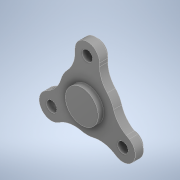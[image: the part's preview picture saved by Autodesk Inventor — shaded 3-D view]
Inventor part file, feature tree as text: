
AUTODESK INVENTOR PART (.ipt)
format: ipt  version: 2022 (Build 260153000, 153)  size: 159,744 bytes
history: mixed  units: in
note: dims shown in document units (in); Inventor stores cm internally (conversion verified against a paired STEP export)
features: extrude x2, sketch x2, chamfer x1, imported_body x1
ambient origin geometry x8: Origin, YZ Plane, XZ Plane, XY Plane, X Axis, Y Axis, Z Axis, Center Point
bodies: Solid1 (imported_parasolid)
feature tree (6):
  extrude  "Extrusion4"  Depth=0.3937in TaperAngle=0.0deg
  extrude  "Extrusion5"  [1 undecoded]
  sketch  "Sketch4"  dims[d8=0.0in d9=0.0in d10=0.3937in d11=0.0in]
  sketch  "Sketch5"
  chamfer  "Chamfer5"  [1 undecoded]
  imported_body  NMx_Import_Brep_tag  [imported B-rep: ~31 faces, bbox_mm=[31.788121, 26.496463, 6.0]]
note: 2 required parameter values undecoded (feature->parameter linkage not recoverable at this tier; creation-order binding heuristic only, values carry confidence <= 0.55)
